# Revit family: Lighting_Pendant_Nordlux_Nori-18-Pendant
name_source: partatom
category: Lighting Fixtures
revit_build: Autodesk Revit 2018 (Build: 20190510_1515(x64)
units: mm (PartAtom-declared; Revit-internal decimal feet)

## family parameters
Cut with Voids When Loaded = No
Host = Face
Light Source = Yes
OmniClass Number = 23.35.47.11
OmniClass Title = Lighting Fixtures
Part Type = Normal
Room Calculation Point = No
Round Connector Dimension = Use Diameter
Shared = No

## types (6) — shared parameters
Apparent Load = 7 VA
BIMobject category = Pendant
Body material = Nordlux  - Wood  - Dark wood
Color Filter = 16777215
Default Elevation = 1219 mm
Description = Nordic minimalism and suspended lightness are the keywords for the Nori pendant series by Danish designers Bjørn + Balle.
Design country = Denmark
Dimming Lamp Color Temperature Shift = <None>
Edition number = 1
IFC Classification = Light Fixture
Installation instructions = https://asset.productmarketingcloud.com
Light bulb material = Nordlux  - Glass  - Glass transparent
Light bulb thread material = Nordlux  - Metal  - Black
Manufacturer = Nordlux
Manufacturer country = China
Manufacturer name = Nordlux
Material main = Metal
Material secondary = Wood
Model = Nori 18
NominalVoltage = 230 V
OmniClass Code = 23-35 47 11
OmniClass Description = Lighting Fixtures
Product Guid = 89cf0a32-a119-45e5-9c2f-6d467a27046e
Product SKU = Nori-18-Pendant
Product data url = https://bimobject.com
Product family = Lighting
Product group = Pendant
Product name = Nori 18 Pendant
Product url = https://nordlux.com
QR code = https://bimobject.com
Tilt Angle = 0.00°
URL = www.nordlux.com
Weight Net (Kg) = 0,58
Youtube clip = https://www.youtube.com

## per-type parameters (varying)
| type | Beam angle | CQS | CRI / Ra | Cord material | EANNumber | Flicker frequency | Peak [cd] | Photometric Web File | Power factor | Shade inner material | Shade material | TM30 Rf | TM30 Rg | Upper body material |
| ART - (2120803001) Finish colour - (White) | 104.40° | 80.6 | 80.3 | Nordlux  - Metal  - White RAL 9016 | 2120803001 | 100 Hz | 165 | Nori 18 Pendant Br. Steel.ies | 0.53 | Nordlux  - Metal  - White RAL 9016 | Nordlux  - Metal  - White RAL 9016 | 84.5 | 94.2 | Nordlux  - Metal  - White RAL 9016 |
| ART - (2120803003) Finish colour - (Black) | 104.40° | 80.6 | 80.3 | Nordlux  - Metal  - Black | 2120803003 | 100 Hz | 165 | Nori 18 Pendant Br. Steel.ies | 0.53 | Nordlux  - Metal  - White RAL 9016 | Nordlux  - Metal  - Black | 84.5 | 94.2 | Nordlux  - Metal  - Black |
| ART - (2120803030) Finish colour - (Copper) | 104.40° | 80.6 | 80.3 | Nordlux  - Metal  - Black | 2120803030 | 100 Hz | 165 | Nori 18 Pendant Br. Steel.ies | 0.53 | Nordlux  - Metal  - Copper | Nordlux  - Metal  - Copper | 84.5 | 94.2 | Nordlux  - Metal  - Black |
| ART - (2120803032) Finish colour - (Brushed steel) | 104.40° | 80.6 | 80.3 | Nordlux  - Metal  - Black | 2120803032 | 100 Hz | 165 | Nori 18 Pendant Br. Steel.ies | 0.53 | Nordlux  - Metal  - Brushed steel | Nordlux  - Metal  - Brushed steel | 84.5 | 94.2 | Nordlux  - Metal  - Black |
| ART - (2120843047) Finish colour - (Smoked glass) | 265.00° | 83 | 83.4 | Nordlux  - Metal  - Black | 2120843047 | 100 Hz | 67.5 | Nori 18 Pen. Smoked glass.ies | 0.53 | Nordlux  - Glass  - Smoked glass | Nordlux  - Glass  - Smoked glass | 86.4 | 96 | Nordlux  - Metal  - Black |
| ART - (2120843001) Finish colour - (Opalwh glass) | 101.50° | 81.3 | 81.2 | Nordlux  - Metal  - White RAL 9016 | 2120843001 | 101 Hz | 145 | Nori 18 Pen. Opalwh glass.ies | 0.54 | Nordlux  - Glass  - Opalwh glass | Nordlux  - Glass  - Opalwh glass | 83.6 | 92.1 | Nordlux  - Metal  - White RAL 9016 |

## geometry (parser evidence)
native form markers: Sweep x4
no freeform markers — native parametric forms only
